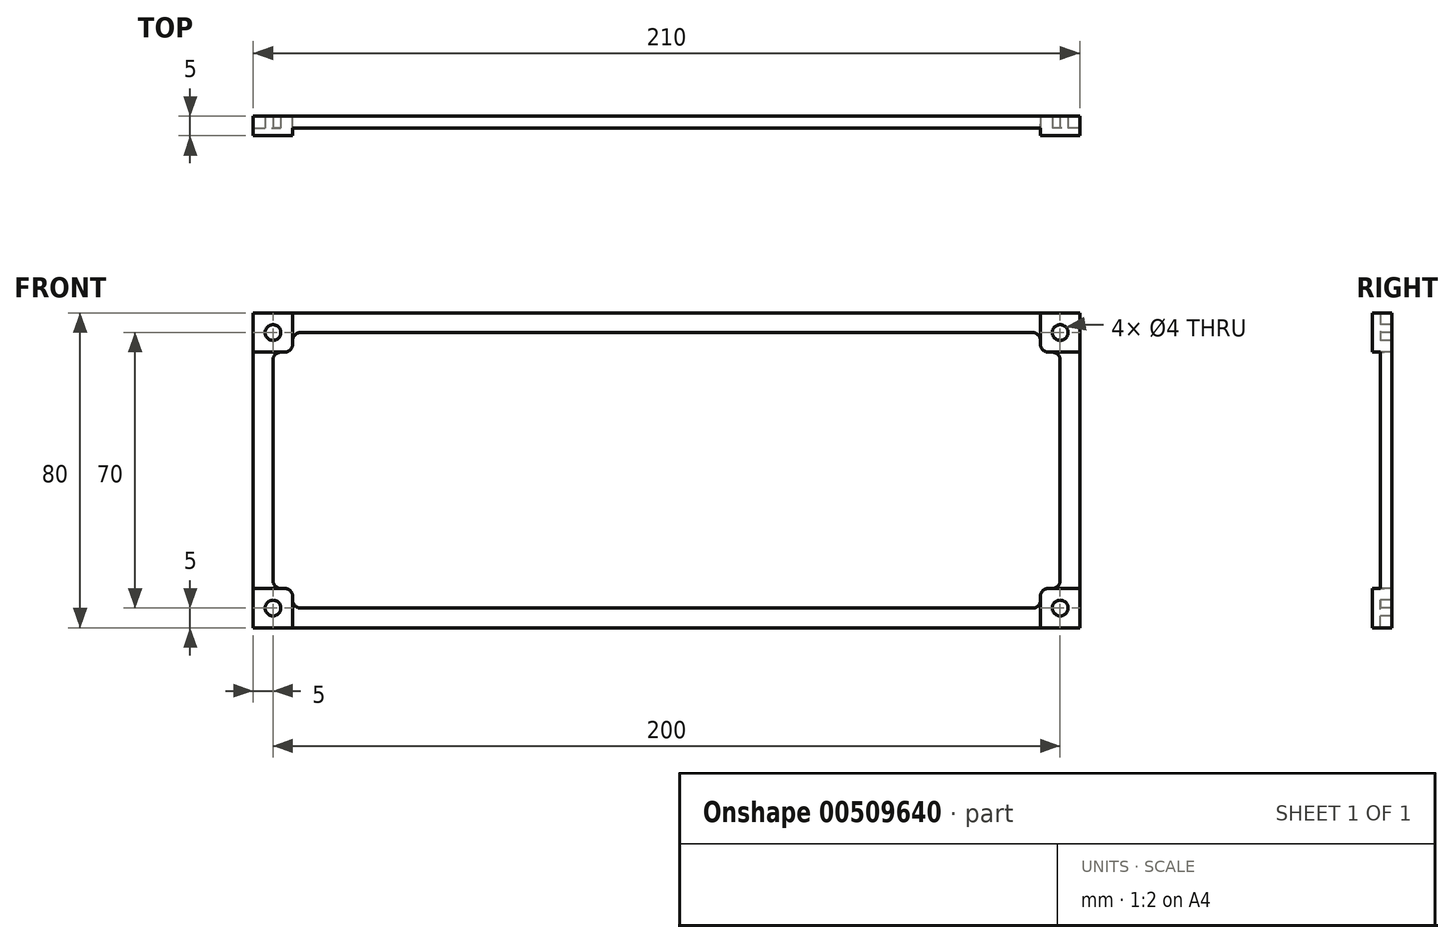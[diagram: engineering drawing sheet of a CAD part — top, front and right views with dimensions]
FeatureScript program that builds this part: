
annotation { "Feature Type Name" : "Feature", "Feature Type Description" : "" }
export const myFeature = defineFeature(function(context is Context, id is Id, definition is map)
    precondition{}
    {
        {
            var Q0;
            Q0=qCreatedBy(makeId("Front.planeOp"),FACE);
            var sketch = newSketch(context, id + "F0", { "sketchPlane" : qUnion([Q0])});
            skLineSegment(sketch, "E0.bottom", {"start": v(105, 40) * mm, "end": v(-105, 40) * mm});
            skLineSegment(sketch, "E0.top", {"start": v(105, -40) * mm, "end": v(-105, -40) * mm});
            skLineSegment(sketch, "E0.left", {"start": v(105, 40) * mm, "end": v(105, -40) * mm});
            skLineSegment(sketch, "E0.right", {"start": v(-105, 40) * mm, "end": v(-105, -40) * mm});
            skPoint(sketch, "E0.middle", {"position": v(0, 0) * mm});
            skSolve(sketch);
        }
        {
            var Q0;
            Q0 = qSketchRegion(id + "F0", true);
            extrude(context, id + "F1", {"entities" : qUnion([Q0]), "depth" : 3 * mm, "offsetDistance" : 25 * mm});
        }
        {
            var Q0;
            Q0=makeQuery(id+"F1.opExtrude","CAP_FACE",FACE,{"disambiguationData":[OSD([sQuery(id+"F0.wireOp",EDGE,"E0.bottom"),sQuery(id+"F0.wireOp",EDGE,"E0.top"),sQuery(id+"F0.wireOp",EDGE,"E0.left"),sQuery(id+"F0.wireOp",EDGE,"E0.right")])],"isStart":false});
            var sketch = newSketch(context, id + "F2", { "sketchPlane" : qUnion([Q0])});
            skLineSegment(sketch, "E1.0", {"start": v(100, 35) * mm, "end": v(-100, 35) * mm, "construction": true});
            skLineSegment(sketch, "E1.1", {"start": v(100, 35) * mm, "end": v(100, -35) * mm, "construction": true});
            skLineSegment(sketch, "E1.2", {"start": v(100, -35) * mm, "end": v(-100, -35) * mm, "construction": true});
            skLineSegment(sketch, "E1.3", {"start": v(-100, 35) * mm, "end": v(-100, -35) * mm, "construction": true});
            skCircle(sketch, "E2", {"center": v(-100, 35) * mm, "radius": 2 * mm});
            skCircle(sketch, "E3", {"center": v(-100, -35) * mm, "radius": 2 * mm});
            skCircle(sketch, "E4", {"center": v(100, -35) * mm, "radius": 2 * mm});
            skCircle(sketch, "E5", {"center": v(100, 35) * mm, "radius": 2 * mm});
            skSolve(sketch);
        }
        {
            var Q0;
            Q0 = qSketchRegion(id + "F2", true);
            extrude(context, id + "F3", {"entities" : qUnion([Q0]), "operationType" : NewBodyOperationType.REMOVE, "oppositeDirection" : true, "depth" : 25 * mm});
        }
        {
            var Q0;
            Q0=makeQuery(id+"F1.opExtrude","CAP_FACE",FACE,{"disambiguationData":[OSD([sQuery(id+"F0.wireOp",EDGE,"E0.bottom"),sQuery(id+"F0.wireOp",EDGE,"E0.top"),sQuery(id+"F0.wireOp",EDGE,"E0.left"),sQuery(id+"F0.wireOp",EDGE,"E0.right")])],"isStart":false});
            var sketch = newSketch(context, id + "F4", { "sketchPlane" : qUnion([Q0])});
            skLineSegment(sketch, "E6.bottom", {"start": v(-105, 40) * mm, "end": v(-95, 40) * mm});
            skLineSegment(sketch, "E6.top", {"start": v(-105, 30) * mm, "end": v(-95, 30) * mm});
            skLineSegment(sketch, "E6.left", {"start": v(-105, 40) * mm, "end": v(-105, 30) * mm});
            skLineSegment(sketch, "E6.right", {"start": v(-95, 40) * mm, "end": v(-95, 30) * mm});
            skLineSegment(sketch, "E7.bottom", {"start": v(-105, -40) * mm, "end": v(-95, -40) * mm});
            skLineSegment(sketch, "E7.top", {"start": v(-105, -30) * mm, "end": v(-95, -30) * mm});
            skLineSegment(sketch, "E7.left", {"start": v(-105, -40) * mm, "end": v(-105, -30) * mm});
            skLineSegment(sketch, "E7.right", {"start": v(-95, -40) * mm, "end": v(-95, -30) * mm});
            skLineSegment(sketch, "E8.bottom", {"start": v(105, -40) * mm, "end": v(95, -40) * mm});
            skLineSegment(sketch, "E8.top", {"start": v(105, -30) * mm, "end": v(95, -30) * mm});
            skLineSegment(sketch, "E8.left", {"start": v(105, -40) * mm, "end": v(105, -30) * mm});
            skLineSegment(sketch, "E8.right", {"start": v(95, -40) * mm, "end": v(95, -30) * mm});
            skLineSegment(sketch, "E9.bottom", {"start": v(105, 40) * mm, "end": v(95, 40) * mm});
            skLineSegment(sketch, "E9.top", {"start": v(105, 30) * mm, "end": v(95, 30) * mm});
            skLineSegment(sketch, "E9.left", {"start": v(105, 40) * mm, "end": v(105, 30) * mm});
            skLineSegment(sketch, "E9.right", {"start": v(95, 40) * mm, "end": v(95, 30) * mm});
            skCircle(sketch, "E10.0", {"center": v(-100, 35) * mm, "radius": 2 * mm});
            skCircle(sketch, "E11.0", {"center": v(-100, -35) * mm, "radius": 2 * mm});
            skCircle(sketch, "E12.0", {"center": v(100, -35) * mm, "radius": 2 * mm});
            skCircle(sketch, "E13.0", {"center": v(100, 35) * mm, "radius": 2 * mm});
            skSolve(sketch);
        }
        {
            var Q0;
            Q0 = qSketchRegion(id + "F4", true);
            extrude(context, id + "F5", {"entities" : qUnion([Q0]), "operationType" : NewBodyOperationType.ADD, "depth" : 2 * mm, "offsetDistance" : 25 * mm});
        }
        {
            var Q0;
            Q0=makeQuery(id+"F1.opExtrude","CAP_FACE",FACE,{"disambiguationData":[OSD([sQuery(id+"F0.wireOp",EDGE,"E0.bottom"),sQuery(id+"F0.wireOp",EDGE,"E0.top"),sQuery(id+"F0.wireOp",EDGE,"E0.left"),sQuery(id+"F0.wireOp",EDGE,"E0.right")])],"isStart":false});
            var sketch = newSketch(context, id + "F6", { "sketchPlane" : qUnion([Q0])});
            skLineSegment(sketch, "E14.bottom", {"start": v(-95, 35) * mm, "end": v(95, 35) * mm});
            skLineSegment(sketch, "E14.top", {"start": v(-95, -35) * mm, "end": v(95, -35) * mm});
            skLineSegment(sketch, "E14.left", {"start": v(-95, 35) * mm, "end": v(-95, -35) * mm});
            skLineSegment(sketch, "E14.right", {"start": v(95, 35) * mm, "end": v(95, -35) * mm});
            skLineSegment(sketch, "E15.bottom", {"start": v(100, 30) * mm, "end": v(95, 30) * mm});
            skLineSegment(sketch, "E15.top", {"start": v(100, -30) * mm, "end": v(95, -30) * mm});
            skLineSegment(sketch, "E15.left", {"start": v(100, 30) * mm, "end": v(100, -30) * mm});
            skLineSegment(sketch, "E15.right", {"start": v(95, 30) * mm, "end": v(95, -30) * mm});
            skLineSegment(sketch, "E16.bottom", {"start": v(-100, 30) * mm, "end": v(-95, 30) * mm});
            skLineSegment(sketch, "E16.top", {"start": v(-100, -30) * mm, "end": v(-95, -30) * mm});
            skLineSegment(sketch, "E16.left", {"start": v(-100, 30) * mm, "end": v(-100, -30) * mm});
            skLineSegment(sketch, "E16.right", {"start": v(-95, 30) * mm, "end": v(-95, -30) * mm});
            skSolve(sketch);
        }
        {
            var Q0;
            Q0 = qSketchRegion(id + "F6", true);
            extrude(context, id + "F7", {"entities" : qUnion([Q0]), "operationType" : NewBodyOperationType.REMOVE, "oppositeDirection" : true, "depth" : 25 * mm, "offsetDistance" : 25 * mm});
        }
        {
            var Q0;
            Q0=makeQuery(id+"F7.boolean.opBoolean","COPY",EDGE,{"derivedFrom":makeQuery(id+"F7.opExtrude","SWEPT_EDGE",EDGE,{"disambiguationData":[OSD([sQuery(id+"F4.wireOp",EDGE,"E6.top"),sQuery(id+"F6.wireOp",EDGE,"E16.bottom"),sQuery(id+"F6.wireOp",EDGE,"E16.left")])]})});
            var Q1;
            Q1=makeQuery(id+"F7.boolean.opBoolean","COPY",EDGE,{"derivedFrom":makeQuery(id+"F7.opExtrude","SWEPT_EDGE",EDGE,{"disambiguationData":[OSD([sQuery(id+"F4.wireOp",EDGE,"E6.right"),sQuery(id+"F6.wireOp",EDGE,"E14.bottom"),sQuery(id+"F6.wireOp",EDGE,"E14.left")])]})});
            var Q2;
            Q2=makeQuery(id+"F7.boolean.opBoolean","MERGE",EDGE,{"derivedFrom":[makeQuery(id+"F5.opExtrude","SWEPT_EDGE",EDGE,{"disambiguationData":[OSD([sQuery(id+"F4.wireOp",EDGE,"E6.top"),sQuery(id+"F4.wireOp",EDGE,"E6.right")])]}),makeQuery(id+"F7.opExtrude","SWEPT_EDGE",EDGE,{"disambiguationData":[OSD([sQuery(id+"F6.wireOp",EDGE,"E14.left"),sQuery(id+"F6.wireOp",EDGE,"E16.bottom"),sQuery(id+"F6.wireOp",EDGE,"E16.right")])]})]});
            var Q3;
            Q3=makeQuery(id+"F7.boolean.opBoolean","COPY",EDGE,{"derivedFrom":makeQuery(id+"F7.opExtrude","SWEPT_EDGE",EDGE,{"disambiguationData":[OSD([sQuery(id+"F4.wireOp",EDGE,"E7.top"),sQuery(id+"F6.wireOp",EDGE,"E16.top"),sQuery(id+"F6.wireOp",EDGE,"E16.left")])]})});
            var Q4;
            Q4=makeQuery(id+"F7.boolean.opBoolean","MERGE",EDGE,{"derivedFrom":[makeQuery(id+"F5.opExtrude","SWEPT_EDGE",EDGE,{"disambiguationData":[OSD([sQuery(id+"F4.wireOp",EDGE,"E7.top"),sQuery(id+"F4.wireOp",EDGE,"E7.right")])]}),makeQuery(id+"F7.opExtrude","SWEPT_EDGE",EDGE,{"disambiguationData":[OSD([sQuery(id+"F6.wireOp",EDGE,"E14.left"),sQuery(id+"F6.wireOp",EDGE,"E16.top"),sQuery(id+"F6.wireOp",EDGE,"E16.right")])]})]});
            var Q5;
            Q5=makeQuery(id+"F7.boolean.opBoolean","COPY",EDGE,{"derivedFrom":makeQuery(id+"F7.opExtrude","SWEPT_EDGE",EDGE,{"disambiguationData":[OSD([sQuery(id+"F4.wireOp",EDGE,"E7.right"),sQuery(id+"F6.wireOp",EDGE,"E14.top"),sQuery(id+"F6.wireOp",EDGE,"E14.left")])]})});
            var Q6;
            Q6=makeQuery(id+"F7.boolean.opBoolean","COPY",EDGE,{"derivedFrom":makeQuery(id+"F7.opExtrude","SWEPT_EDGE",EDGE,{"disambiguationData":[OSD([sQuery(id+"F4.wireOp",EDGE,"E9.right"),sQuery(id+"F6.wireOp",EDGE,"E14.bottom"),sQuery(id+"F6.wireOp",EDGE,"E14.right")])]})});
            var Q7;
            Q7=makeQuery(id+"F7.boolean.opBoolean","MERGE",EDGE,{"derivedFrom":[makeQuery(id+"F5.opExtrude","SWEPT_EDGE",EDGE,{"disambiguationData":[OSD([sQuery(id+"F4.wireOp",EDGE,"E9.top"),sQuery(id+"F4.wireOp",EDGE,"E9.right")])]}),makeQuery(id+"F7.opExtrude","SWEPT_EDGE",EDGE,{"disambiguationData":[OSD([sQuery(id+"F6.wireOp",EDGE,"E14.right"),sQuery(id+"F6.wireOp",EDGE,"E15.bottom"),sQuery(id+"F6.wireOp",EDGE,"E15.right")])]})]});
            var Q8;
            Q8=makeQuery(id+"F7.boolean.opBoolean","COPY",EDGE,{"derivedFrom":makeQuery(id+"F7.opExtrude","SWEPT_EDGE",EDGE,{"disambiguationData":[OSD([sQuery(id+"F4.wireOp",EDGE,"E9.top"),sQuery(id+"F6.wireOp",EDGE,"E15.bottom"),sQuery(id+"F6.wireOp",EDGE,"E15.left")])]})});
            var Q9;
            Q9=makeQuery(id+"F7.boolean.opBoolean","COPY",EDGE,{"derivedFrom":makeQuery(id+"F7.opExtrude","SWEPT_EDGE",EDGE,{"disambiguationData":[OSD([sQuery(id+"F4.wireOp",EDGE,"E8.right"),sQuery(id+"F6.wireOp",EDGE,"E14.top"),sQuery(id+"F6.wireOp",EDGE,"E14.right")])]})});
            var Q10;
            Q10=makeQuery(id+"F7.boolean.opBoolean","MERGE",EDGE,{"derivedFrom":[makeQuery(id+"F5.opExtrude","SWEPT_EDGE",EDGE,{"disambiguationData":[OSD([sQuery(id+"F4.wireOp",EDGE,"E8.top"),sQuery(id+"F4.wireOp",EDGE,"E8.right")])]}),makeQuery(id+"F7.opExtrude","SWEPT_EDGE",EDGE,{"disambiguationData":[OSD([sQuery(id+"F6.wireOp",EDGE,"E14.right"),sQuery(id+"F6.wireOp",EDGE,"E15.top"),sQuery(id+"F6.wireOp",EDGE,"E15.right")])]})]});
            var Q11;
            Q11=makeQuery(id+"F7.boolean.opBoolean","COPY",EDGE,{"derivedFrom":makeQuery(id+"F7.opExtrude","SWEPT_EDGE",EDGE,{"disambiguationData":[OSD([sQuery(id+"F4.wireOp",EDGE,"E8.top"),sQuery(id+"F6.wireOp",EDGE,"E15.top"),sQuery(id+"F6.wireOp",EDGE,"E15.left")])]})});
            fillet(context, id + "F8", {"entities" : qUnion([Q0, Q1, Q2, Q3, Q4, Q5, Q6, Q7, Q8, Q9, Q10, Q11]), "radius" : 2 * mm, "tangentPropagation" : true, "allowEdgeOverflow" : false});
        }
    });
